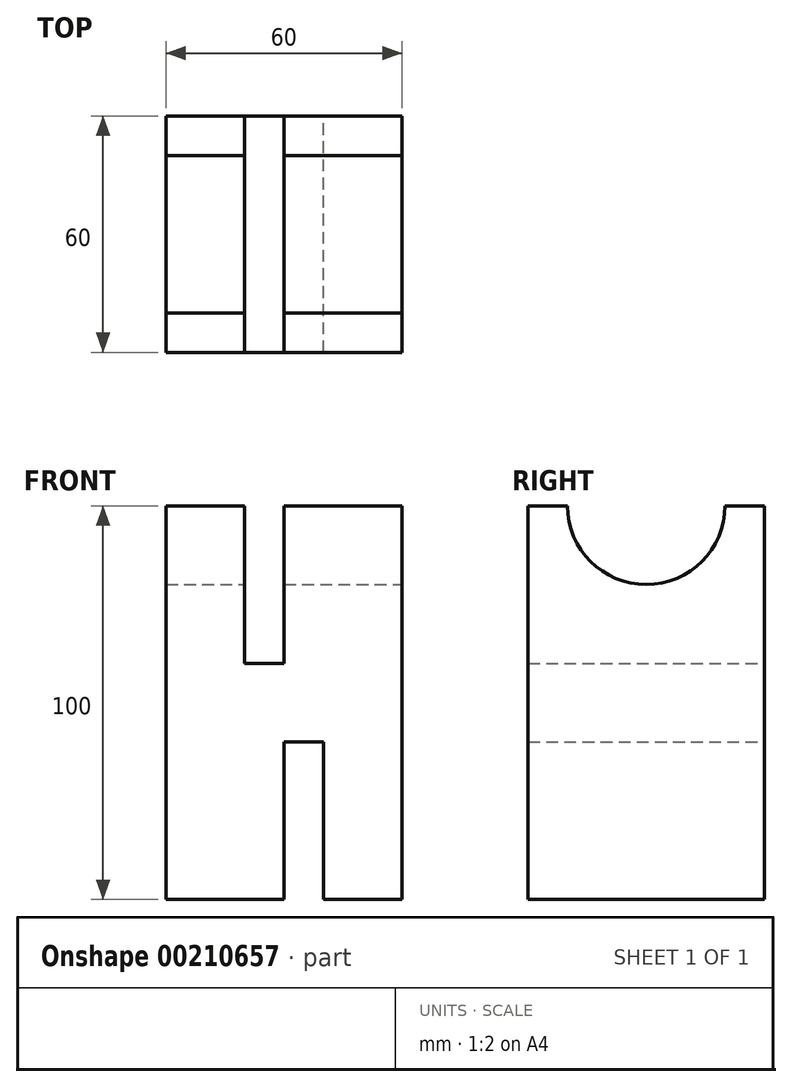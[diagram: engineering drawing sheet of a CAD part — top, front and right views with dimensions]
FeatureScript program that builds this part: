
annotation { "Feature Type Name" : "Feature", "Feature Type Description" : "" }
export const myFeature = defineFeature(function(context is Context, id is Id, definition is map)
    precondition{}
    {
        {
            var Q0;
            Q0=qCreatedBy(makeId("Front.planeOp"),FACE);
            var sketch = newSketch(context, id + "F0", { "sketchPlane" : qUnion([Q0])});
            skLineSegment(sketch, "E0", {"start": v(-60, 82.62) * mm, "end": v(-60, -17.38) * mm});
            skLineSegment(sketch, "E1", {"start": v(-60, -17.38) * mm, "end": v(-30, -17.38) * mm});
            skLineSegment(sketch, "E2", {"start": v(-30, -17.38) * mm, "end": v(-30, 22.62) * mm});
            skLineSegment(sketch, "E3", {"start": v(-30, 22.62) * mm, "end": v(-20, 22.62) * mm});
            skLineSegment(sketch, "E4", {"start": v(-20, 22.62) * mm, "end": v(-20, -17.38) * mm});
            skLineSegment(sketch, "E5", {"start": v(-20, -17.38) * mm, "end": v(0, -17.38) * mm});
            skLineSegment(sketch, "E6", {"start": v(0, -17.38) * mm, "end": v(0, 82.62) * mm});
            skLineSegment(sketch, "E7", {"start": v(0, 82.62) * mm, "end": v(-30, 82.62) * mm});
            skLineSegment(sketch, "E8", {"start": v(-30, 82.62) * mm, "end": v(-30, 42.62) * mm});
            skLineSegment(sketch, "E9", {"start": v(-30, 42.62) * mm, "end": v(-40, 42.62) * mm});
            skLineSegment(sketch, "E10", {"start": v(-40, 42.62) * mm, "end": v(-40, 82.62) * mm});
            skLineSegment(sketch, "E11", {"start": v(-40, 82.62) * mm, "end": v(-60, 82.62) * mm});
            skSolve(sketch);
        }
        {
            var Q0;
            Q0=makeQuery(id+"F0.imprint","IMPRINT",FACE,{"disambiguationData":[TD([[makeQuery(id+"F0.imprint","IMPRINT",EDGE,{"derivedFrom":sQuery(id+"F0.wireOp",EDGE,"E0")}),1.0]])]});
            extrude(context, id + "F1", {"entities" : qUnion([Q0]), "depth" : 60 * mm});
        }
        {
            var Q0;
            Q0=makeQuery(id+"F1.opExtrude","SWEPT_FACE",FACE,{"disambiguationData":[OSD([sQuery(id+"F0.wireOp",EDGE,"E6")])]});
            var sketch = newSketch(context, id + "F2", { "sketchPlane" : qUnion([Q0])});
            skArc(sketch, "E12", {"start": v(-50, 82.62) * mm, "mid": v(-44.14, 68.48) * mm, "end": v(-30, 62.62) * mm});
            skArc(sketch, "E13", {"start": v(-10, 82.62) * mm, "mid": v(-15.86, 68.48) * mm, "end": v(-30, 62.62) * mm});
            skLineSegment(sketch, "E14", {"start": v(-50, 82.62) * mm, "end": v(-10, 82.62) * mm});
            skSolve(sketch);
        }
        {
            var Q0;
            Q0=makeQuery(id+"F2.imprint","IMPRINT",FACE,{"disambiguationData":[TD([[makeQuery(id+"F2.imprint","IMPRINT",EDGE,{"derivedFrom":sQuery(id+"F2.wireOp",EDGE,"E12")}),1.0]])]});
            extrude(context, id + "F3", {"entities" : qUnion([Q0]), "operationType" : NewBodyOperationType.REMOVE, "oppositeDirection" : true, "depth" : 60 * mm});
        }
    });
